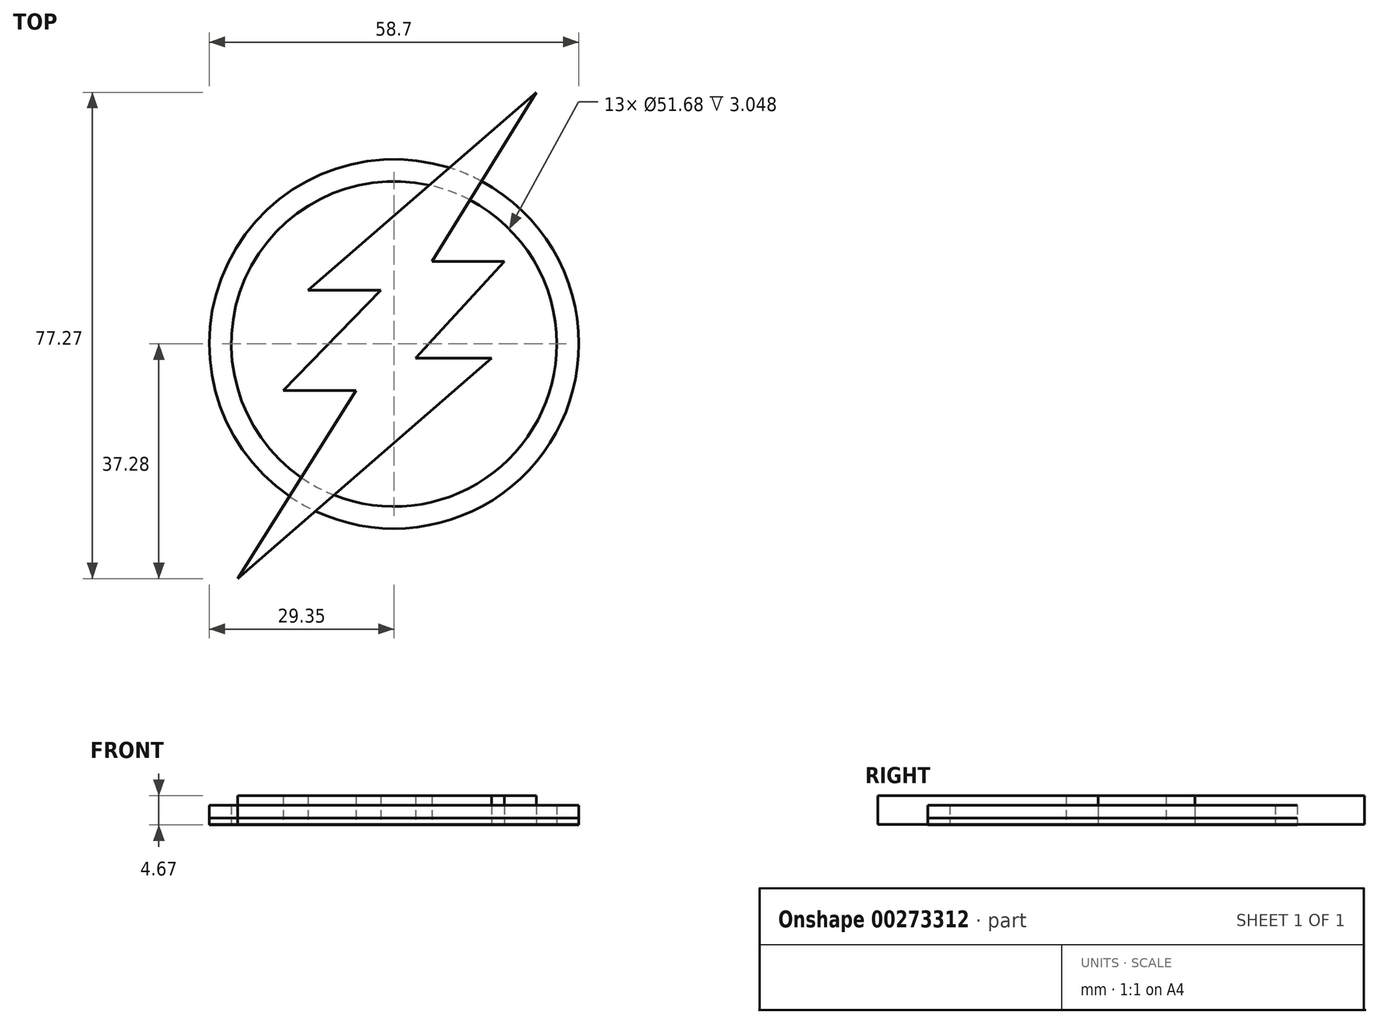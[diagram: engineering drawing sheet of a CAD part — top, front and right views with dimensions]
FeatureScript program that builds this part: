
annotation { "Feature Type Name" : "Feature", "Feature Type Description" : "" }
export const myFeature = defineFeature(function(context is Context, id is Id, definition is map)
    precondition{}
    {
        {
            var Q0;
            Q0=qCreatedBy(makeId("Top.planeOp"),FACE);
            var sketch = newSketch(context, id + "F0", { "sketchPlane" : qUnion([Q0])});
            skCircle(sketch, "E0", {"center": v(0, 0) * mm, "radius": 25.84 * mm});
            skSolve(sketch);
        }
        {
            var Q0;
            Q0=makeQuery(id+"F0.imprint","IMPRINT",FACE,{"disambiguationData":[TD([[makeQuery(id+"F0.imprint","IMPRINT",EDGE,{"derivedFrom":sQuery(id+"F0.wireOp",EDGE,"E0")}),1.0]])]});
            var sketch = newSketch(context, id + "F1", { "sketchPlane" : qUnion([Q0])});
            skCircle(sketch, "E1", {"center": v(0, 0) * mm, "radius": 29.35 * mm});
            skSolve(sketch);
        }
        {
            var Q0;
            Q0=qCreatedBy(makeId("Top.planeOp"),FACE);
            var sketch = newSketch(context, id + "F2", { "sketchPlane" : qUnion([Q0])});
            skLineSegment(sketch, "E2", {"start": v(22.6, 40) * mm, "end": v(-13.65, 8.53) * mm});
            skLineSegment(sketch, "E3", {"start": v(-13.65, 8.53) * mm, "end": v(-2.09, 8.53) * mm});
            skLineSegment(sketch, "E4", {"start": v(-2.09, 8.53) * mm, "end": v(-17.62, -7.4) * mm});
            skLineSegment(sketch, "E5", {"start": v(-17.62, -7.4) * mm, "end": v(-6.03, -7.4) * mm});
            skLineSegment(sketch, "E6", {"start": v(-6.03, -7.4) * mm, "end": v(-24.87, -37.28) * mm});
            skLineSegment(sketch, "E7", {"start": v(-24.87, -37.28) * mm, "end": v(15.46, -2.28) * mm});
            skLineSegment(sketch, "E8", {"start": v(15.46, -2.28) * mm, "end": v(3.41, -2.28) * mm});
            skLineSegment(sketch, "E9", {"start": v(3.41, -2.28) * mm, "end": v(17.5, 13.08) * mm});
            skLineSegment(sketch, "E10", {"start": v(17.5, 13.08) * mm, "end": v(6.04, 13.08) * mm});
            skLineSegment(sketch, "E11", {"start": v(6.04, 13.08) * mm, "end": v(22.6, 40) * mm});
            skSolve(sketch);
        }
        {
            var Q0;
            Q0=sQuery(id+"F1.wireOp",EDGE,"E1");
            extrude(context, id + "F3", {"bodyType" : ToolBodyType.SURFACE, "surfaceEntities" : qUnion([Q0]), "depth" : 3 * mm});
        }
        {
            var Q0;
            Q0=sQuery(id+"F0.wireOp",EDGE,"E0");
            extrude(context, id + "F4", {"bodyType" : ToolBodyType.SURFACE, "surfaceEntities" : qUnion([Q0]), "depth" : 3 * mm});
        }
        {
            var Q0;
            Q0=makeQuery(id+"F1.imprint","IMPRINT",FACE,{"disambiguationData":[TD([[makeQuery(id+"F1.imprint","IMPRINT",EDGE,{"derivedFrom":makeQuery(id+"F0.imprint","IMPRINT",EDGE,{"derivedFrom":sQuery(id+"F0.wireOp",EDGE,"E0")})}),1.0]])]});
            var Q1;
            Q1=makeQuery(id+"F1.imprint","IMPRINT",FACE,{"disambiguationData":[TD([[makeQuery(id+"F1.imprint","IMPRINT",EDGE,{"derivedFrom":sQuery(id+"F1.wireOp",EDGE,"E1")}),1.0]])]});
            extrude(context, id + "F5", {"entities" : qUnion([Q0, Q1]), "depth" : 1 * mm});
        }
        {
            var Q0;
            Q0=makeQuery(id+"F1.imprint","IMPRINT",FACE,{"disambiguationData":[TD([[makeQuery(id+"F1.imprint","IMPRINT",EDGE,{"derivedFrom":sQuery(id+"F1.wireOp",EDGE,"E1")}),1.0]])]});
            var Q1;
            Q1=makeQuery(id+"F1.imprint","IMPRINT",FACE,{"disambiguationData":[TD([[makeQuery(id+"F1.imprint","IMPRINT",EDGE,{"derivedFrom":makeQuery(id+"F0.imprint","IMPRINT",EDGE,{"derivedFrom":sQuery(id+"F0.wireOp",EDGE,"E0")})}),1.0]])]});
            extrude(context, id + "F6", {"entities" : qUnion([Q0, Q1]), "oppositeDirection" : true, "depth" : 0.1 * mm});
        }
        {
            var Q0;
            Q0=makeQuery(id+"F1.imprint","IMPRINT",FACE,{"disambiguationData":[TD([[makeQuery(id+"F1.imprint","IMPRINT",EDGE,{"derivedFrom":sQuery(id+"F1.wireOp",EDGE,"E1")}),1.0]])]});
            extrude(context, id + "F7", {"entities" : qUnion([Q0]), "depth" : 3.05 * mm});
        }
        {
            var Q0;
            Q0=qSketchRegion(id+"F2",true);
            extrude(context, id + "F8", {"entities" : qUnion([Q0]), "depth" : 4.57 * mm});
        }
    });
